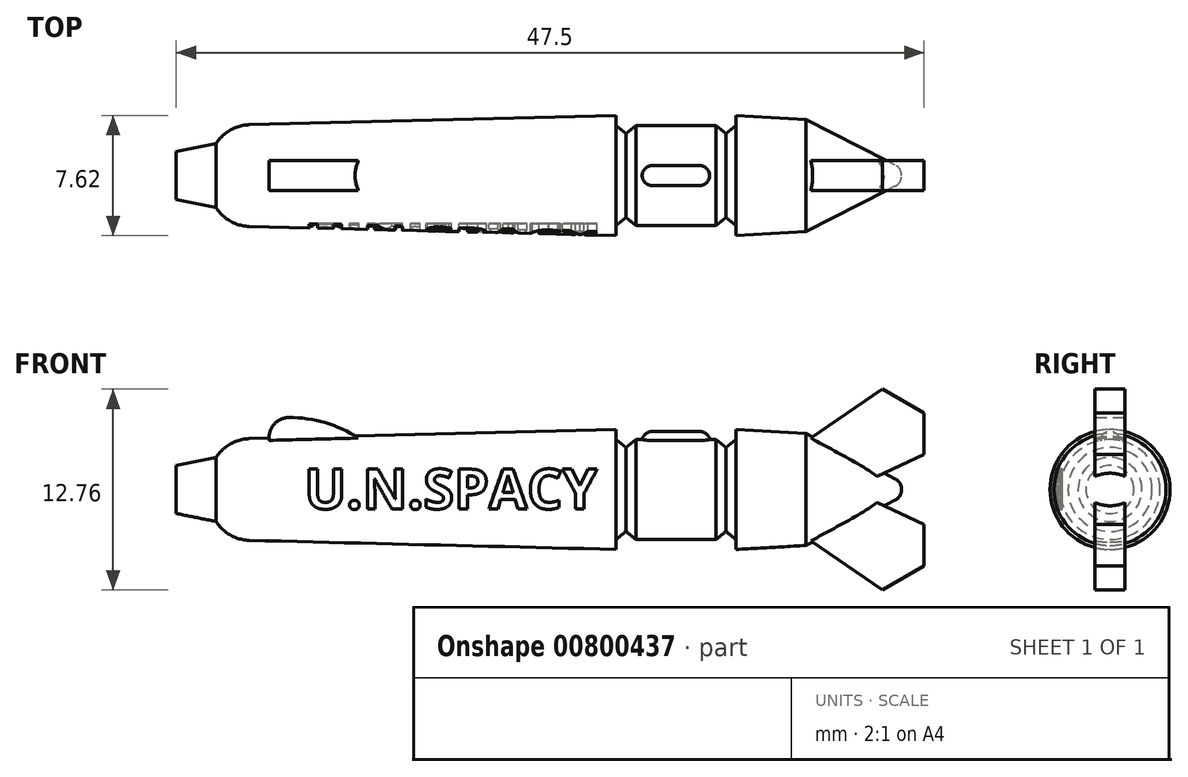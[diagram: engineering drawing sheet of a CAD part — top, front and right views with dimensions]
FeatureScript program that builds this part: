
annotation { "Feature Type Name" : "Feature", "Feature Type Description" : "" }
export const myFeature = defineFeature(function(context is Context, id is Id, definition is map)
    precondition{}
    {
        {
            var Q0;
            Q0=qCreatedBy(makeId("Front.planeOp"),FACE);
            var sketch = newSketch(context, id + "F0", { "sketchPlane" : qUnion([Q0])});
            skLineSegment(sketch, "E0", {"start": v(-36.83, 0) * mm, "end": v(32.69, 0) * mm, "construction": true});
            skLineSegment(sketch, "E1", {"start": v(-27.93, 0) * mm, "end": v(-27.93, 1.52) * mm});
            skLineSegment(sketch, "E2", {"start": v(-27.93, 1.52) * mm, "end": v(-25.4, 2.03) * mm});
            skLineSegment(sketch, "E3", {"start": v(-25.4, 2.03) * mm, "end": v(-25.4, 3.18) * mm});
            skLineSegment(sketch, "E4", {"start": v(-25.4, 3.18) * mm, "end": v(0, 3.81) * mm});
            skLineSegment(sketch, "E5", {"start": v(0, 3.81) * mm, "end": v(0, 3.17) * mm});
            skLineSegment(sketch, "E6", {"start": v(1.27, 3.18) * mm, "end": v(6.35, 3.18) * mm});
            skLineSegment(sketch, "E7", {"start": v(6.99, 2.67) * mm, "end": v(7.62, 3.18) * mm});
            skLineSegment(sketch, "E8", {"start": v(7.62, 3.18) * mm, "end": v(7.62, 3.81) * mm});
            skLineSegment(sketch, "E9", {"start": v(7.62, 3.81) * mm, "end": v(12.07, 3.56) * mm});
            skLineSegment(sketch, "E10", {"start": v(12.07, 3.56) * mm, "end": v(17.73, 0.68) * mm});
            skLineSegment(sketch, "E11", {"start": v(18.14, 0) * mm, "end": v(-27.93, 0) * mm});
            skArc(sketch, "E12", {"start": v(18.14, 0) * mm, "mid": v(18.03, 0.4) * mm, "end": v(17.73, 0.68) * mm});
            skLineSegment(sketch, "E13", {"start": v(6.35, 3.18) * mm, "end": v(6.99, 2.67) * mm});
            skLineSegment(sketch, "E14", {"start": v(3.81, 3.18) * mm, "end": v(3.81, 0) * mm, "construction": true});
            skLineSegment(sketch, "E15.MirrorCS", {"start": v(1.27, 3.18) * mm, "end": v(0.64, 2.67) * mm});
            skLineSegment(sketch, "E16.MirrorCS", {"start": v(0.64, 2.67) * mm, "end": v(0, 3.18) * mm});
            skPoint(sketch, "E17.end.orphan", {"position": v(6.35, 2.16) * mm});
            skPoint(sketch, "E18.orphan", {"position": v(1.27, 2.16) * mm});
            skSolve(sketch);
        }
        {
            var Q0;
            Q0=qSketchRegion(id+"F0",true);
            var Q1;
            Q1=sQuery(id+"F0.wireOp",EDGE,"E11");
            revolve(context, id + "F1", {"entities" : qUnion([Q0]), "axis" : qUnion([Q1]), "revolveType" : RevolveType.FULL});
        }
        {
            var Q0;
            Q0=makeQuery(id+"F1.opRevolve","SWEPT_EDGE",EDGE,{"disambiguationData":[OSD([sQuery(id+"F0.wireOp",EDGE,"E3"),sQuery(id+"F0.wireOp",EDGE,"E4")])]});
            fillet(context, id + "F2", {"entities" : qUnion([Q0]), "radius" : 2.54 * mm, "allowEdgeOverflow" : false});
        }
        {
            var Q0;
            Q0=qCreatedBy(makeId("Front.planeOp"),FACE);
            var sketch = newSketch(context, id + "F3", { "sketchPlane" : qUnion([Q0])});
            skArc(sketch, "E19", {"start": v(-20.77, 4.57) * mm, "mid": v(-22.03, 3.36) * mm, "end": v(-20.88, 2.04) * mm});
            skArc(sketch, "E20", {"start": v(-14.92, 2.04) * mm, "mid": v(-17.58, 3.92) * mm, "end": v(-20.77, 4.57) * mm});
            skLineSegment(sketch, "E21", {"start": v(-20.88, 2.04) * mm, "end": v(-14.92, 2.04) * mm});
            skPoint(sketch, "E22.orphan", {"position": v(12.68, 0) * mm});
            skLineSegment(sketch, "E23", {"start": v(11.6, 2.73) * mm, "end": v(16.93, 6.38) * mm});
            skLineSegment(sketch, "E24", {"start": v(16.93, 6.38) * mm, "end": v(19.57, 4.86) * mm});
            skLineSegment(sketch, "E25", {"start": v(19.57, 4.86) * mm, "end": v(19.57, 2.23) * mm});
            skLineSegment(sketch, "E26", {"start": v(19.57, 2.23) * mm, "end": v(15.53, 0.34) * mm});
            skLineSegment(sketch, "E27", {"start": v(11.6, 2.73) * mm, "end": v(14.4, 0.34) * mm});
            skLineSegment(sketch, "E28", {"start": v(14.8, 0) * mm, "end": v(12.68, 0) * mm, "construction": true});
            skLineSegment(sketch, "E29.MirrorCS", {"start": v(11.6, -2.73) * mm, "end": v(14.4, -0.34) * mm});
            skLineSegment(sketch, "E30.MirrorCS", {"start": v(11.6, -2.73) * mm, "end": v(16.93, -6.38) * mm});
            skLineSegment(sketch, "E31.MirrorCS", {"start": v(19.57, -4.86) * mm, "end": v(19.57, -2.23) * mm});
            skLineSegment(sketch, "E32.MirrorCS", {"start": v(19.57, -2.23) * mm, "end": v(15.53, -0.34) * mm});
            skLineSegment(sketch, "E33", {"start": v(14.4, 0.34) * mm, "end": v(15.53, 0.34) * mm});
            skPoint(sketch, "E34.MirrorCS.end.orphan", {"position": v(19.57, -4.86) * mm});
            skPoint(sketch, "E34.MirrorCS.start.orphan", {"position": v(16.93, -6.38) * mm});
            skLineSegment(sketch, "E35.MirrorCS", {"start": v(14.4, -0.34) * mm, "end": v(15.53, -0.34) * mm});
            skPoint(sketch, "E36.orphan", {"position": v(14.8, 0) * mm});
            skLineSegment(sketch, "E37.MirrorCS", {"start": v(16.93, -6.38) * mm, "end": v(19.57, -4.86) * mm});
            skSolve(sketch);
        }
        {
            var Q0;
            Q0=qSketchRegion(id+"F3",true);
            extrude(context, id + "F4", {"entities" : qUnion([Q0]), "operationType" : NewBodyOperationType.ADD, "endBound" : BoundingType.SYMMETRIC, "depth" : 1.9 * mm, "offsetDistance" : 25.4 * mm});
        }
        {
            var Q0;
            Q0=qCreatedBy(makeId("Front.planeOp"),FACE);
            cPlane(context, id + "F5", {"entities" : qUnion([Q0]), "cplaneType" : CPlaneType.OFFSET, "offset" : 3.05 * mm, "width" : 152.4 * mm, "height" : 152.4 * mm});
        }
        {
            var Q0;
            Q0=qCreatedBy(id+"F5.planeOp",FACE);
            var sketch = newSketch(context, id + "F6", { "sketchPlane" : qUnion([Q0])});
            skText(sketch, "E38", { "text": "U.N.SPACY", "fontName": "OpenSans-Bold.ttf"});
            const initialGuessF6  = {"E38": [-0.01978, -0.00123, 1, 0, 0.00254]};
            skSetInitialGuess(sketch, initialGuessF6);
            skSolve(sketch);
        }
        {
            var Q0;
            Q0=qSketchRegion(id+"F6",true);
            extrude(context, id + "F7", {"entities" : qUnion([Q0]), "operationType" : NewBodyOperationType.REMOVE, "depth" : 25.4 * mm, "offsetDistance" : 25.4 * mm});
        }
        {
            var Q0;
            Q0=qCreatedBy(makeId("Front.planeOp"),FACE);
            var sketch = newSketch(context, id + "F8", { "sketchPlane" : qUnion([Q0])});
            skArc(sketch, "E39", {"start": v(2.29, 3.68) * mm, "mid": v(1.84, 3.5) * mm, "end": v(1.65, 3.05) * mm});
            skLineSegment(sketch, "E40", {"start": v(1.65, 3.05) * mm, "end": v(5.97, 3.05) * mm});
            skLineSegment(sketch, "E41", {"start": v(3.81, 4.43) * mm, "end": v(3.81, -0.67) * mm, "construction": true});
            skArc(sketch, "E42.MirrorC", {"start": v(5.33, 3.68) * mm, "mid": v(5.78, 3.5) * mm, "end": v(5.97, 3.05) * mm});
            skLineSegment(sketch, "E43", {"start": v(2.29, 3.68) * mm, "end": v(5.33, 3.68) * mm});
            skSolve(sketch);
        }
        {
            var Q0;
            Q0=makeQuery(id+"F8.imprint","IMPRINT",FACE,{"disambiguationData":[TD([[makeQuery(id+"F8.imprint","IMPRINT",EDGE,{"derivedFrom":sQuery(id+"F8.wireOp",EDGE,"E39")}),1.0]])]});
            var Q1;
            Q1=sQuery(id+"F8.wireOp",EDGE,"E40");
            revolve(context, id + "F9", {"operationType" : NewBodyOperationType.ADD, "surfaceOperationType" : NewSurfaceOperationType.NEW, "entities" : qUnion([Q0]), "axis" : qUnion([Q1]), "revolveType" : RevolveType.FULL});
        }
    });
